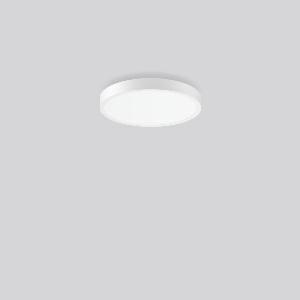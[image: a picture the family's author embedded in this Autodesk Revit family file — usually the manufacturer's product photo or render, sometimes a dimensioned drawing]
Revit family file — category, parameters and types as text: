
# Revit family: triona_round_a_312420_002_1_76_2d57
name_source: partatom
category: Lighting Fixtures
units: mm (PartAtom-declared; Revit-internal decimal feet)

## family parameters
Cut with Voids When Loaded = No
Host = Face
Light Source = No
Part Type = Normal
Room Calculation Point = No
Round Connector Dimension = Use Diameter
Shared = No

## types (1)
- TRIONA round A (1 x LED Modul 840, 6050 lm, 4000)
    Apparent Load = 64 VA
    CIE Flux Codes = 49 80 96 82 100
    Color Rendering = 80
    Color Temperature = 4000
    Default Elevation = 1800 mm
    Description = Series: TRIONA round
Decorative round LED surface-mounted luminaire. Flat, seamless frame: aluminium extrusion profile, powder coated. Cover made of sheet steel, powder-coated. Direct light emission through a diffuser plastic opal. Indirect light emission through a flush diffuser made of satin-finish plastic. Lightguide and diffuser made of non-yellowing plastic (PMMA). Lateral light emission (RZB SIDELITE technology) for above-average homogeneous light distribution. Direct 70%, indirect 30% light emission. Suitable for Ceiling mounting, Wall (surface). Tool-free mounting via bayonet connection. Electronic ballast included. Very easy installation thanks to Plug+Play connection. 
Colour: traffic white, matt (RAL 9016)
Diameter: 461 mm
Height: 88 mm
Lamp: LED
Socket: without socket
Colour temperature: 4000K
Colour rendering index (CRI): 80
System power: 64 W
Rated luminous flux: 6050 lm
Luminous efficiency: 95 lm/W
Control gear: Converter, dimmable, DALI
Protection class: I
Type of protection: IP 20
    Height = 88 mm
    Lamp = 1 x LED Modul 840
    Lamp Light Flux = 6050 lm
    Lamp count = 1
    Length = 461 mm
    Lifetime = 50000 h
    Luminous efficacy = 95 lm/W
    Manufacturer = RZB
    ModVariant = No
    Model = 312420.002.1.76
    Mounting Place = Ceiling
    Mounting Type = Surface mounted
    Number of Poles = 1
    OnlyDefault = Yes
    Power Factor = 1
    Product Name = TRIONA round A
    Product group = Surface mounted modular luminaires
    ProductGroupID = 306
    Protection Class = Protection class I
    Protection Degree = IP 20
    RLX_Detail_Level = 1
    RLX_Emergency_Light_Flux = 0 lm
    RLX_Emergency_Type = 0
    RLX_Emergency_Type_DB = No
    RlxData = <blob elided: 36989 chars, md5=30492f20>
    Socket = socket
    Standby Power = 0 W
    System Light Flux = 6050 lm
    System Power = 64 W
    Type Comments = Product without accessories
    Type Image = 312420.002.jpg
    URL = http://relux.com
    VarID = ---
    Voltage = 230 V
    Voltage Range = 220-240 V
    Weight = 0.00 kg
    Width = 0 mm  [stored 0 ft]

note: [stored X ft] marks values corroborated as IEEE doubles in the binary element streams (Revit-internal decimal feet)

## geometry (parser evidence)
native form markers: Blend x4, Sweep x12
no freeform markers — native parametric forms only
